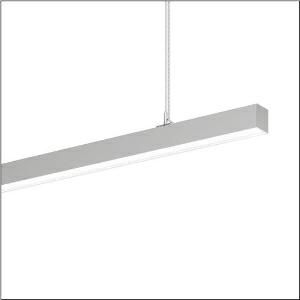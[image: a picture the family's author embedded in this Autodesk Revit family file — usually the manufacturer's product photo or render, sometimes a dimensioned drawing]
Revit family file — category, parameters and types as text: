
# Revit family: silica_21_51mx30tbt5s
name_source: partatom
category: Lighting Fixtures
units: mm (PartAtom-declared; Revit-internal decimal feet)

## family parameters
Cut with Voids When Loaded = No
Host = Face
Light Source = No
Part Type = Normal
Room Calculation Point = No
Round Connector Dimension = Use Diameter
Shared = No

## types (1)
- --- (1 x LED, 5150 lm, 42.2 W, 6500K)
    Apparent Load = 42 VA
    CIE Flux Codes = 47 79 96 58 100
    Color Rendering = 80
    Color Temperature = 6500K
    Default Elevation = 1800 mm
    Description = Silica 21, office luminaire, primary optical cover: cover, of PMMA, opal, light emission: direct/indirect distribution, primary light characteristic: symmetric, installation type: suspended mounting, LED, rated luminous flux: 5.150lm, luminous efficacy: 116lm/W, light colour: 8tw, colour temperature: 2700..6500K, control gear: DALI DT8, with terminal, 3+2-pole, max. 2.5mm², mains connection: 220..240V, AC, 50/60Hz, rated input power: 44.3W, luminaire housing, of aluminium, metallic grey (RAL 9006), length: 1.504mm, width: 53mm, height: 53mm, protection rating (complete): IP20, insulation class (complete): insulation class I (protective earthing), certification: CE, permissible operating ambient temperature: 0..+35°C, standard: EN 50419, packaging unit: 1 piece
    Height = 53 mm
    Lamp = 1 x LED
    Lamp Light Flux = 5150 lm
    Lamp Power = 42.2 W
    Lamp count = 1
    Length = 1504 mm
    Luminous efficacy = 122 lm/W
    Manufacturer = Siteco
    ModVariant = No
    Model = 51MX30TBT5S
    Mounting Place = Ceiling
    Mounting Type = Pendant
    Number of Poles = 1
    OnlyDefault = Yes
    Power Factor = 1
    Product Name = Silica 21
    Product group = office luminaire | ceiling pendant
    ProductGroupID = 903
    Protection Class = Protection class I
    Protection Degree = IP 20
    RLX_Detail_Level = 1
    RLX_Emergency_Light_Flux = 0 lm
    RLX_Emergency_Type = 0
    RLX_Emergency_Type_DB = No
    RlxData = <blob elided: 20137 chars, md5=888179a4>
    Socket = socket
    Standby Power = 0 W
    System Light Flux = 5150 lm
    System Power = 42 W
    Type Comments = individual setting
    Type Image = l_1335864.jpg
    URL = http://relux.com
    VarID = @adj_140665
    Voltage = 0 V
    Weight = 0.00 kg
    Width = 53 mm

## geometry (parser evidence)
native form markers: Blend x4, Sweep x12
no freeform markers — native parametric forms only
